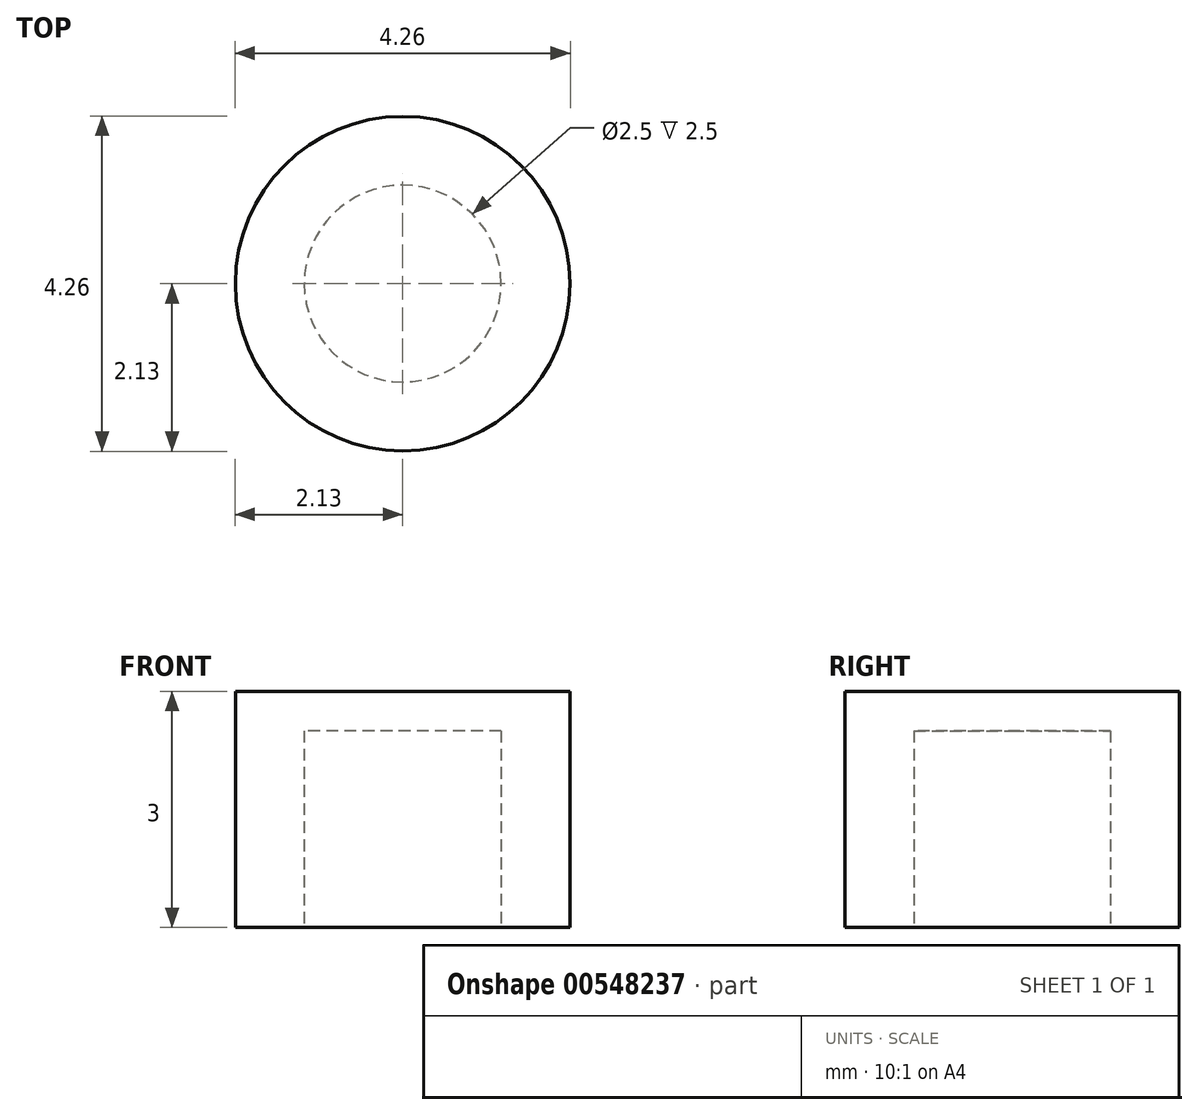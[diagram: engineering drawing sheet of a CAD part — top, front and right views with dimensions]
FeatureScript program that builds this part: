
annotation { "Feature Type Name" : "Feature", "Feature Type Description" : "" }
export const myFeature = defineFeature(function(context is Context, id is Id, definition is map)
    precondition{}
    {
        {
            assignVariable(context, id + "F0", {"name" : "Height", "anyValue" : 3});
        }
        {
            assignVariable(context, id + "F1", {"name" : "InnerHeight", "anyValue" : 2.5});
        }
        {
            var Q0;
            Q0=qCreatedBy(makeId("Top.planeOp"),FACE);
            var sketch = newSketch(context, id + "F2", { "sketchPlane" : qUnion([Q0])});
            skCircle(sketch, "E0", {"center": v(0, 0) * mm, "radius": 2.12 * mm});
            skCircle(sketch, "E1", {"center": v(0, 0) * mm, "radius": 1.25 * mm});
            skSolve(sketch);
        }
        {
            var Q0;
            Q0=makeQuery(id+"F2.imprint","IMPRINT",FACE,{"disambiguationData":[TD([[makeQuery(id+"F2.imprint","IMPRINT",EDGE,{"derivedFrom":sQuery(id+"F2.wireOp",EDGE,"E0")}),1.0]])]});
            var Q1;
            Q1=makeQuery(id+"F2.imprint","IMPRINT",FACE,{"disambiguationData":[TD([[makeQuery(id+"F2.imprint","IMPRINT",EDGE,{"derivedFrom":sQuery(id+"F2.wireOp",EDGE,"E1")}),1.0]])]});
            extrude(context, id + "F3", {"entities" : qUnion([Q0, Q1]), "depth" : (getVariable(context, 'Height')) * mm, "offsetDistance" : 25 * mm});
        }
        {
            var Q0;
            Q0=makeQuery(id+"F2.imprint","IMPRINT",FACE,{"disambiguationData":[TD([[makeQuery(id+"F2.imprint","IMPRINT",EDGE,{"derivedFrom":sQuery(id+"F2.wireOp",EDGE,"E1")}),1.0]])]});
            extrude(context, id + "F4", {"entities" : qUnion([Q0]), "operationType" : NewBodyOperationType.REMOVE, "depth" : (getVariable(context, 'InnerHeight')) * mm, "offsetDistance" : 25 * mm});
        }
    });
